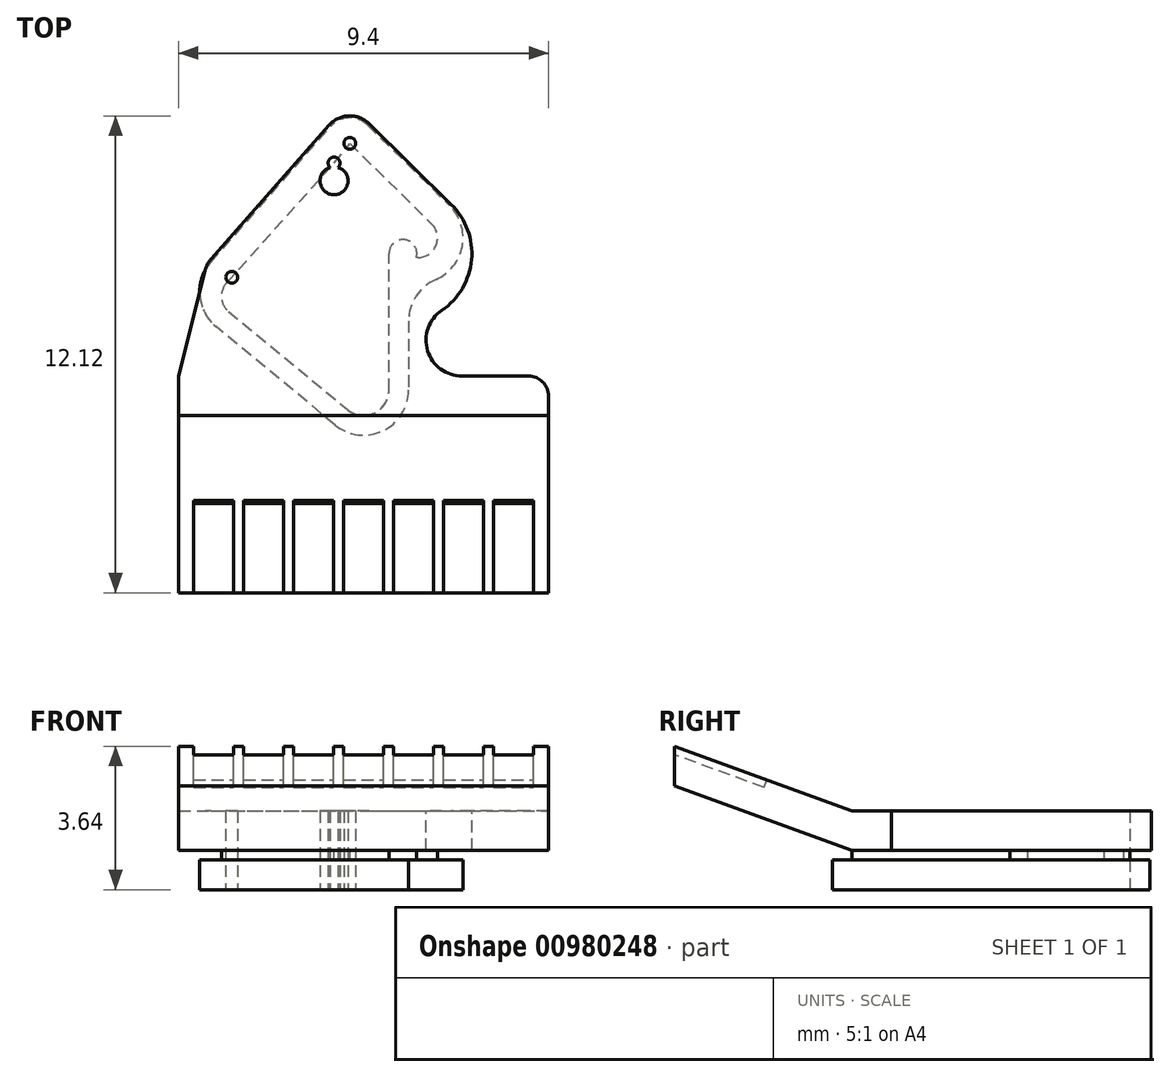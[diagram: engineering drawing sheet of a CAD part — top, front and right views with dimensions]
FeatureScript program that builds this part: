
annotation { "Feature Type Name" : "Feature", "Feature Type Description" : "" }
export const myFeature = defineFeature(function(context is Context, id is Id, definition is map)
    precondition{}
    {
        {
            assignVariable(context, id + "F0", {"name" : "top_height", "anyValue" : 1 * mm});
        }
        {
            assignVariable(context, id + "F1", {"name" : "foot_height", "anyValue" : 0.75 * mm});
        }
        {
            assignVariable(context, id + "F2", {"name" : "total_height", "anyValue" : 2 * mm});
        }
        {
            var Q0;
            Q0=qCreatedBy(makeId("Top.planeOp"),FACE);
            var sketch = newSketch(context, id + "F3", { "sketchPlane" : qUnion([Q0])});
            skCircle(sketch, "E0", {"center": v(-3.35, -1) * mm, "radius": 0.15 * mm});
            skCircle(sketch, "E1", {"center": v(-0.75, 1.9) * mm, "radius": 0.15 * mm});
            skCircle(sketch, "E2", {"center": v(-0.35, 2.4) * mm, "radius": 0.15 * mm});
            skCircle(sketch, "E3", {"center": v(-0.75, 1.45) * mm, "radius": 0.35 * mm});
            skCircle(sketch, "E4", {"center": v(2.5, -2.6) * mm, "radius": 0.85 * mm});
            skSolve(sketch);
        }
        {
            var Q0;
            Q0=qSketchRegion(id+"F3",true);
            extrude(context, id + "F4", {"entities" : qUnion([Q0]), "offsetDistance" : 25 * mm, "depth" : getVariable(context, 'total_height')});
        }
        {
            var Q0;
            Q0=makeQuery(id+"F4.opExtrude","CAP_FACE",FACE,{"disambiguationData":[OSD([sQuery(id+"F3.wireOp",EDGE,"E4")])],"isStart":false});
            var sketch = newSketch(context, id + "F5", { "sketchPlane" : qUnion([Q0])});
            skArc(sketch, "E5", {"start": v(2.23, 0.85) * mm, "mid": v(2.74, -0.56) * mm, "end": v(1.99, -1.85) * mm});
            skArc(sketch, "E6", {"start": v(1.99, -1.85) * mm, "mid": v(1.63, -2.87) * mm, "end": v(2.5, -3.51) * mm});
            skArc(sketch, "E7", {"start": v(0.14, 2.9) * mm, "mid": v(-0.37, 3.1) * mm, "end": v(-0.87, 2.86) * mm});
            skArc(sketch, "E8", {"start": v(-4.03, -0.83) * mm, "mid": v(-3.97, -0.67) * mm, "end": v(-3.87, -0.54) * mm});
            skLineSegment(sketch, "E9", {"start": v(-3.87, -0.54) * mm, "end": v(-0.87, 2.86) * mm});
            skLineSegment(sketch, "E10", {"start": v(0.14, 2.9) * mm, "end": v(2.23, 0.85) * mm});
            skLineSegment(sketch, "E11", {"start": v(-4.7, -4.51) * mm, "end": v(4.7, -4.51) * mm});
            skLineSegment(sketch, "E12", {"start": v(-4.7, -4.51) * mm, "end": v(-4.7, -3.51) * mm});
            skLineSegment(sketch, "E13", {"start": v(-4.7, -3.51) * mm, "end": v(-4.03, -0.83) * mm});
            skLineSegment(sketch, "E14", {"start": v(4.7, -4.51) * mm, "end": v(4.7, -4.01) * mm});
            skLineSegment(sketch, "E15", {"start": v(4.2, -3.51) * mm, "end": v(2.5, -3.51) * mm});
            skPoint(sketch, "E16.visualSharp", {"position": v(4.7, -3.51) * mm});
            skArc(sketch, "E16.filletArc", {"start": v(4.7, -4.01) * mm, "mid": v(4.55, -3.66) * mm, "end": v(4.2, -3.51) * mm});
            skLineSegment(sketch, "E17", {"start": v(4.7, -3.51) * mm, "end": v(4.7, -4.51) * mm, "construction": true});
            skSolve(sketch);
        }
        {
            var Q0;
            Q0=qSketchRegion(id+"F5",true);
            extrude(context, id + "F6", {"entities" : qUnion([Q0]), "oppositeDirection" : true, "depth" : getVariable(context, 'top_height')});
        }
        {
            var Q0;
            Q0=makeQuery(id+"F6.opExtrude","CAP_FACE",FACE,{"disambiguationData":[OSD([sQuery(id+"F5.wireOp",EDGE,"E5"),sQuery(id+"F5.wireOp",EDGE,"E6"),sQuery(id+"F5.wireOp",EDGE,"E7"),sQuery(id+"F5.wireOp",EDGE,"E8"),sQuery(id+"F5.wireOp",EDGE,"E9"),sQuery(id+"F5.wireOp",EDGE,"E10"),sQuery(id+"F5.wireOp",EDGE,"E11"),sQuery(id+"F5.wireOp",EDGE,"E12"),sQuery(id+"F5.wireOp",EDGE,"E13"),sQuery(id+"F5.wireOp",EDGE,"E14"),sQuery(id+"F5.wireOp",EDGE,"E15"),sQuery(id+"F5.wireOp",EDGE,"E16.filletArc")])],"isStart":false});
            var sketch = newSketch(context, id + "F7", { "sketchPlane" : qUnion([Q0])});
            skArc(sketch, "E18", {"start": v(-0.41, 4.36) * mm, "mid": v(0.27, 4.45) * mm, "end": v(0.64, 3.87) * mm});
            skLineSegment(sketch, "E19", {"start": v(0.64, 3.87) * mm, "end": v(0.64, 0.4) * mm});
            skArc(sketch, "E20", {"start": v(0.64, 0.4) * mm, "mid": v(1.05, 0.05) * mm, "end": v(1.34, 0.5) * mm});
            skLineSegment(sketch, "E21", {"start": v(-3.48, 1.15) * mm, "end": v(-0.75, -1.9) * mm});
            skPoint(sketch, "E22", {"position": v(-3.35, 1) * mm});
            skPoint(sketch, "E23", {"position": v(-0.75, -1.9) * mm});
            skPoint(sketch, "E24", {"position": v(-0.35, -2.4) * mm});
            skLineSegment(sketch, "E25", {"start": v(-0.75, -1.9) * mm, "end": v(-0.35, -2.4) * mm});
            skArc(sketch, "E26", {"start": v(-3.48, 1.15) * mm, "mid": v(-3.6, 1.52) * mm, "end": v(-3.43, 1.87) * mm});
            skLineSegment(sketch, "E27", {"start": v(-3.43, 1.87) * mm, "end": v(-0.41, 4.36) * mm});
            skArc(sketch, "E28", {"start": v(1.38, 0.5) * mm, "mid": v(1.84, 0.19) * mm, "end": v(1.73, -0.36) * mm});
            skLineSegment(sketch, "E29", {"start": v(-0.35, -2.4) * mm, "end": v(1.73, -0.36) * mm});
            skLineSegment(sketch, "E30", {"start": v(1.38, 0.5) * mm, "end": v(1.34, 0.5) * mm});
            skSolve(sketch);
        }
        {
            var Q0;
            Q0=qSketchRegion(id+"F7",true);
            extrude(context, id + "F8", {"entities" : qUnion([Q0]), "depth" : getVariable(context, 'total_height') - getVariable(context, 'top_height') - getVariable(context, 'foot_height')});
        }
        {
            var Q0;
            Q0=makeQuery(id+"F8.opExtrude","CAP_FACE",FACE,{"disambiguationData":[OSD([sQuery(id+"F7.wireOp",EDGE,"E18"),sQuery(id+"F7.wireOp",EDGE,"E19"),sQuery(id+"F7.wireOp",EDGE,"E20"),sQuery(id+"F7.wireOp",EDGE,"E21"),sQuery(id+"F7.wireOp",EDGE,"E25"),sQuery(id+"F7.wireOp",EDGE,"E26"),sQuery(id+"F7.wireOp",EDGE,"E27"),sQuery(id+"F7.wireOp",EDGE,"E28"),sQuery(id+"F7.wireOp",EDGE,"E29"),sQuery(id+"F7.wireOp",EDGE,"E30")])],"isStart":false});
            var sketch = newSketch(context, id + "F9", { "sketchPlane" : qUnion([Q0])});
            skLineSegment(sketch, "E31", {"start": v(-3.88, 0.62) * mm, "end": v(-0.84, -2.83) * mm});
            skLineSegment(sketch, "E32", {"start": v(0.1, -2.86) * mm, "end": v(2.18, -0.82) * mm});
            skLineSegment(sketch, "E33", {"start": v(1.14, 2.1) * mm, "end": v(1.14, 3.87) * mm});
            skLineSegment(sketch, "E34", {"start": v(-0.73, 4.75) * mm, "end": v(-3.75, 2.25) * mm});
            skArc(sketch, "E35.filletArc", {"start": v(-3.75, 2.25) * mm, "mid": v(-4.16, 1.46) * mm, "end": v(-3.88, 0.62) * mm});
            skPoint(sketch, "E36.visualSharp", {"position": v(1.14, 6.3) * mm});
            skArc(sketch, "E36.filletArc", {"start": v(1.15, 3.87) * mm, "mid": v(0.49, 4.9) * mm, "end": v(-0.73, 4.75) * mm});
            skArc(sketch, "E37.filletArc", {"start": v(2.18, -0.82) * mm, "mid": v(2.5, 0.2) * mm, "end": v(1.84, 1.05) * mm});
            skArc(sketch, "E38.filletArc", {"start": v(1.14, 2.1) * mm, "mid": v(1.33, 1.48) * mm, "end": v(1.84, 1.05) * mm});
            skPoint(sketch, "E39.visualSharp", {"position": v(-0.38, -3.34) * mm});
            skArc(sketch, "E39.filletArc", {"start": v(-0.84, -2.83) * mm, "mid": v(-0.37, -3.05) * mm, "end": v(0.1, -2.86) * mm});
            skSolve(sketch);
        }
        {
            var Q0;
            Q0=qSketchRegion(id+"F9",true);
            extrude(context, id + "F10", {"entities" : qUnion([Q0]), "depth" : getVariable(context, 'foot_height')});
        }
        {
            var Q0;
            Q0=makeQuery(id+"F4.opExtrude","SWEPT_BODY",BODY,{"disambiguationData":[OSD([sQuery(id+"F3.wireOp",EDGE,"E4")])]});
            var Q1;
            Q1=makeQuery(id+"F10.opExtrude","SWEPT_BODY",BODY,{"disambiguationData":[OSD([sQuery(id+"F9.wireOp",EDGE,"E31"),sQuery(id+"F9.wireOp",EDGE,"E32"),sQuery(id+"F9.wireOp",EDGE,"E33"),sQuery(id+"F9.wireOp",EDGE,"E34"),sQuery(id+"F9.wireOp",EDGE,"E35.filletArc"),sQuery(id+"F9.wireOp",EDGE,"E36.filletArc"),sQuery(id+"F9.wireOp",EDGE,"E37.filletArc"),sQuery(id+"F9.wireOp",EDGE,"E38.filletArc"),sQuery(id+"F9.wireOp",EDGE,"E39.filletArc")])]});
            booleanBodies(context, id + "F11", {"operationType" : BooleanOperationType.SUBTRACTION, "tools" : qUnion([Q0]), "targets" : qUnion([Q1])});
        }
        {
            var Q0;
            Q0=qCreatedBy(makeId("Right.planeOp"),FACE);
            var sketch = newSketch(context, id + "F12", { "sketchPlane" : qUnion([Q0])});
            skLineSegment(sketch, "E40", {"start": v(-9.02, 3.64) * mm, "end": v(-4.51, 2) * mm});
            skSolve(sketch);
        }
        {
            var Q0;
            Q0=makeQuery(id+"F6.opExtrude","SWEPT_FACE",FACE,{"disambiguationData":[OSD([sQuery(id+"F5.wireOp",EDGE,"E11")])]});
            var Q1;
            Q1=sQuery(id+"F12.wireOp",EDGE,"E40");
            sweep(context, id + "F13", {"operationType" : NewBodyOperationType.ADD, "profiles" : qUnion([Q0]), "path" : qUnion([Q1]), "keepProfileOrientation" : true});
        }
        {
            var Q0;
            {var subQ0=sQuery(id+"F12.wireOp",EDGE,"E40");var subQ1=sQuery(id+"F5.wireOp",EDGE,"E11");Q0=makeQuery(id+"F13.opSweep","SWEPT_FACE",FACE,{"disambiguationData":[OSD([subQ1,subQ0]),TDD([makeQuery(id+"F6.opExtrude","CAP_EDGE",EDGE,{"disambiguationData":[OSD([subQ1])],"isStart":true}),subQ0])]});}
            var sketch = newSketch(context, id + "F14", { "sketchPlane" : qUnion([Q0])});
            skLineSegment(sketch, "E41.bottom", {"start": v(-4.32, -7.22) * mm, "end": v(-3.3, -7.22) * mm});
            skLineSegment(sketch, "E41.top", {"start": v(-4.32, -9.72) * mm, "end": v(-3.3, -9.72) * mm});
            skLineSegment(sketch, "E41.left", {"start": v(-4.32, -7.22) * mm, "end": v(-4.32, -9.72) * mm});
            skLineSegment(sketch, "E41.right", {"start": v(-3.3, -7.22) * mm, "end": v(-3.3, -9.72) * mm});
            skLineSegment(sketch, "E42.1.0.0", {"start": v(-3.05, -7.22) * mm, "end": v(-3.05, -9.72) * mm});
            skLineSegment(sketch, "E42.1.0.1", {"start": v(-3.05, -7.22) * mm, "end": v(-2.03, -7.22) * mm});
            skLineSegment(sketch, "E42.1.0.2", {"start": v(-2.03, -7.22) * mm, "end": v(-2.03, -9.72) * mm});
            skLineSegment(sketch, "E42.1.0.3", {"start": v(-3.05, -9.72) * mm, "end": v(-2.03, -9.72) * mm});
            skLineSegment(sketch, "E42.2.0.0", {"start": v(-1.78, -7.22) * mm, "end": v(-1.78, -9.72) * mm});
            skLineSegment(sketch, "E42.2.0.1", {"start": v(-1.78, -7.22) * mm, "end": v(-0.76, -7.22) * mm});
            skLineSegment(sketch, "E42.2.0.2", {"start": v(-0.76, -7.22) * mm, "end": v(-0.76, -9.72) * mm});
            skLineSegment(sketch, "E42.2.0.3", {"start": v(-1.78, -9.72) * mm, "end": v(-0.76, -9.72) * mm});
            skLineSegment(sketch, "E42.3.0.0", {"start": v(-0.51, -7.22) * mm, "end": v(-0.51, -9.72) * mm});
            skLineSegment(sketch, "E42.3.0.1", {"start": v(-0.51, -7.22) * mm, "end": v(0.51, -7.22) * mm});
            skLineSegment(sketch, "E42.3.0.2", {"start": v(0.51, -7.22) * mm, "end": v(0.51, -9.72) * mm});
            skLineSegment(sketch, "E42.3.0.3", {"start": v(-0.51, -9.72) * mm, "end": v(0.51, -9.72) * mm});
            skLineSegment(sketch, "E42.4.0.0", {"start": v(0.76, -7.22) * mm, "end": v(0.76, -9.72) * mm});
            skLineSegment(sketch, "E42.4.0.1", {"start": v(0.76, -7.22) * mm, "end": v(1.78, -7.22) * mm});
            skLineSegment(sketch, "E42.4.0.2", {"start": v(1.78, -7.22) * mm, "end": v(1.78, -9.72) * mm});
            skLineSegment(sketch, "E42.4.0.3", {"start": v(0.76, -9.72) * mm, "end": v(1.78, -9.72) * mm});
            skLineSegment(sketch, "E42.5.0.0", {"start": v(2.03, -7.22) * mm, "end": v(2.03, -9.72) * mm});
            skLineSegment(sketch, "E42.5.0.1", {"start": v(2.03, -7.22) * mm, "end": v(3.05, -7.22) * mm});
            skLineSegment(sketch, "E42.5.0.2", {"start": v(3.05, -7.22) * mm, "end": v(3.05, -9.72) * mm});
            skLineSegment(sketch, "E42.5.0.3", {"start": v(2.03, -9.72) * mm, "end": v(3.05, -9.72) * mm});
            skLineSegment(sketch, "E42.6.0.0", {"start": v(3.3, -7.22) * mm, "end": v(3.3, -9.72) * mm});
            skLineSegment(sketch, "E42.6.0.1", {"start": v(3.3, -7.22) * mm, "end": v(4.32, -7.22) * mm});
            skLineSegment(sketch, "E42.6.0.2", {"start": v(4.32, -7.22) * mm, "end": v(4.32, -9.72) * mm});
            skLineSegment(sketch, "E42.6.0.3", {"start": v(3.3, -9.72) * mm, "end": v(4.32, -9.72) * mm});
            skLineSegment(sketch, "E42.direction1", {"start": v(-4.32, -9.72) * mm, "end": v(-3.05, -9.72) * mm, "construction": true});
            skSolve(sketch);
        }
        {
            var Q0;
            Q0=qSketchRegion(id+"F14",true);
            extrude(context, id + "F15", {"entities" : qUnion([Q0]), "operationType" : NewBodyOperationType.REMOVE, "oppositeDirection" : true, "depth" : 0.2 * mm});
        }
    });
